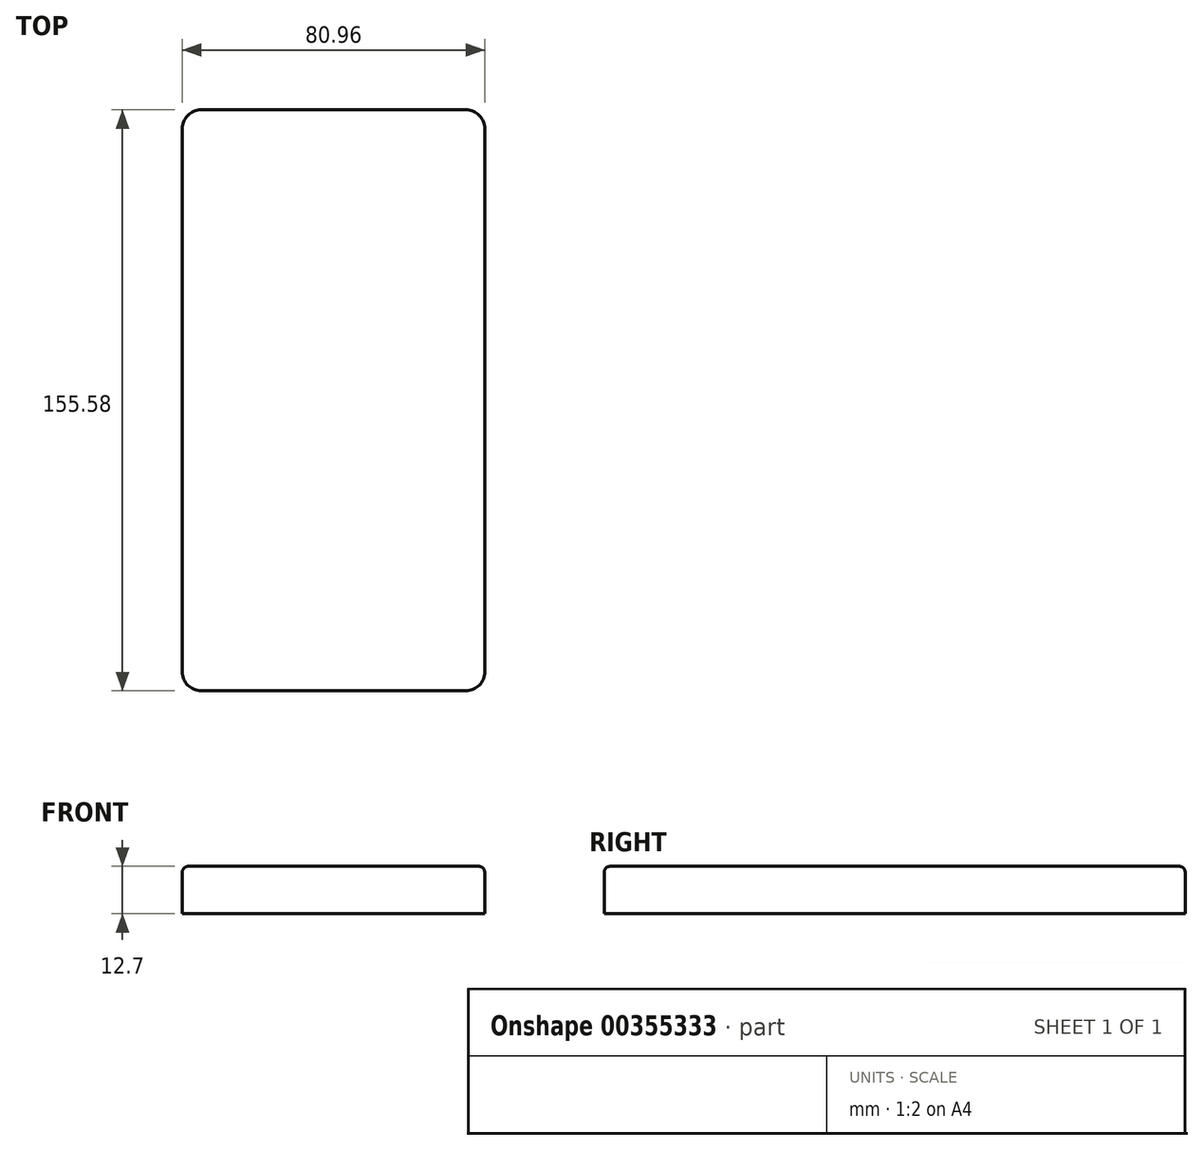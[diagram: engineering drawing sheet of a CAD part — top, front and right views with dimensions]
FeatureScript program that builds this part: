
annotation { "Feature Type Name" : "Feature", "Feature Type Description" : "" }
export const myFeature = defineFeature(function(context is Context, id is Id, definition is map)
    precondition{}
    {
        {
            var Q0;
            Q0=qCreatedBy(makeId("Top.planeOp"),FACE);
            var sketch = newSketch(context, id + "F0", { "sketchPlane" : qUnion([Q0])});
            skLineSegment(sketch, "E0.bottom", {"start": v(40.48, -77.79) * mm, "end": v(-40.48, -77.79) * mm});
            skLineSegment(sketch, "E0.top", {"start": v(40.48, 77.79) * mm, "end": v(-40.48, 77.79) * mm});
            skLineSegment(sketch, "E0.left", {"start": v(40.48, -77.79) * mm, "end": v(40.48, 77.79) * mm});
            skLineSegment(sketch, "E0.right", {"start": v(-40.48, -77.79) * mm, "end": v(-40.48, 77.79) * mm});
            skPoint(sketch, "E0.middle", {"position": v(0, 0) * mm});
            skSolve(sketch);
        }
        {
            var Q0;
            Q0=makeQuery(id+"F0.imprint","IMPRINT",FACE,{"disambiguationData":[TD([[makeQuery(id+"F0.imprint","IMPRINT",EDGE,{"derivedFrom":sQuery(id+"F0.wireOp",EDGE,"E0.bottom")}),-1.0]])]});
            extrude(context, id + "F1", {"entities" : qUnion([Q0]), "depth" : 12.7 * mm, "symmetric" : true});
        }
        {
            var Q0;
            Q0=makeQuery(id+"F1.opExtrude","SWEPT_EDGE",EDGE,{"disambiguationData":[OSD([sQuery(id+"F0.wireOp",EDGE,"E0.bottom"),sQuery(id+"F0.wireOp",EDGE,"E0.left")])]});
            var Q1;
            Q1=makeQuery(id+"F1.opExtrude","SWEPT_EDGE",EDGE,{"disambiguationData":[OSD([sQuery(id+"F0.wireOp",EDGE,"E0.bottom"),sQuery(id+"F0.wireOp",EDGE,"E0.right")])]});
            var Q2;
            Q2=makeQuery(id+"F1.opExtrude","SWEPT_EDGE",EDGE,{"disambiguationData":[OSD([sQuery(id+"F0.wireOp",EDGE,"E0.top"),sQuery(id+"F0.wireOp",EDGE,"E0.left")])]});
            var Q3;
            Q3=makeQuery(id+"F1.opExtrude","SWEPT_EDGE",EDGE,{"disambiguationData":[OSD([sQuery(id+"F0.wireOp",EDGE,"E0.top"),sQuery(id+"F0.wireOp",EDGE,"E0.right")])]});
            fillet(context, id + "F2", {"entities" : qUnion([Q0, Q1, Q2, Q3]), "radius" : 5.08 * mm, "tangentPropagation" : true, "allowEdgeOverflow" : false});
        }
        {
            var Q0;
            Q0=makeQuery(id+"F1.opExtrude","CAP_EDGE",EDGE,{"disambiguationData":[OSD([sQuery(id+"F0.wireOp",EDGE,"E0.top")])],"isStart":false});
            fillet(context, id + "F3", {"entities" : qUnion([Q0]), "radius" : 1.59 * mm, "tangentPropagation" : true, "allowEdgeOverflow" : false});
        }
    });
